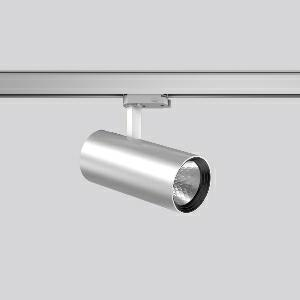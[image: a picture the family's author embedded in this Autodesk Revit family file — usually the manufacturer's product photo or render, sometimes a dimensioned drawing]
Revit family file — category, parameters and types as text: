
# Revit family: deecos_s_mini_742195_004_76_3da2
name_source: partatom
category: Lighting Fixtures
units: mm (PartAtom-declared; Revit-internal decimal feet)

## family parameters
Cut with Voids When Loaded = No
Host = Face
Light Source = No
Part Type = Normal
Room Calculation Point = No
Round Connector Dimension = Use Diameter
Shared = No

## types (1)
- DEECOS S mini (1 x LED Modul 930, 2500 lm, 3000)
    Apparent Load = 20 VA
    Approval mark = CE
    CIE Flux Codes = 100 100 100 100 100
    Color Rendering = 90
    Color Temperature = 3000
    Default Elevation = 1800 mm
    Description = Series: DEECOS S mini
LED surface-mounted projector in modern design with no visible cooling ribs. Housing: die-cast aluminium, powder-coated. Rotation range: 356°. Swivel range: 90°. Black plastic ring and recessed LED to prevent glare from the side. Optical assembly with reflector made of MIRO-Silver with 98% total light reflection for outstanding efficiency - can be changed without tools. Best colour rendering index Ra>90. With adapter for RZB 3-circuit DALI tracks. Suitable for Track on ceiling, Wall track. High quality converter without flickering and stroboscopic effect. The following accessories can be mounted without use of tools: interchangeable lenses, decorative glasses, honeycomb louvre, clear and frosted diffusers, white interchangeable plastic ring. 
Colour: silver
Diameter: 87 mm
Height: 214 mm
Lamp: LED
Socket: without socket
Colour temperature: 3000K
Colour rendering index (CRI): 92
System power: 20 W
Rated luminous flux: 2500 lm
Luminous efficiency: 125 lm/W
Control gear: Converter, dimmable, DALI
Protection class: I
Type of protection: IP 20
    Height = 214 mm
    Lamp = 1 x LED Modul 930
    Lamp Light Flux = 2500 lm
    Lamp count = 1
    Length = 87 mm
    Lifetime = 50000 h
    Luminous efficacy = 125 lm/W
    Manufacturer = RZB
    ModVariant = No
    Model = 742195.004.76
    Mounting Place = Ceiling
    Mounting Type = Rail mounted
    Number of Poles = 1
    OnlyDefault = Yes
    Power Factor = 1
    Product Name = DEECOS S mini
    Product group = Track mounted projectors
    ProductGroupID = 301
    Protection Class = Protection class I
    Protection Degree = IP 20
    RLX_Detail_Level = 1
    RLX_Emergency_Light_Flux = 0 lm
    RLX_Emergency_Type = 0
    RLX_Emergency_Type_DB = No
    RlxData = <blob elided: 37273 chars, md5=b440883b>
    Socket = socket
    Standby Power = 0 W
    System Light Flux = 2500 lm
    System Power = 20 W
    Type Comments = Product without accessories
    Type Image = 741926.004.jpg
    URL = http://relux.com
    VarID = ---
    Voltage = 230 V
    Voltage Range = 220-240 V
    Weight = 0.00 kg
    Width = 0 mm  [stored 0 ft]

note: [stored X ft] marks values corroborated as IEEE doubles in the binary element streams (Revit-internal decimal feet)

## geometry (parser evidence)
native form markers: Blend x4, Sweep x14
no freeform markers — native parametric forms only
